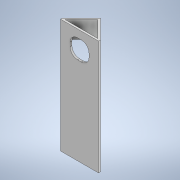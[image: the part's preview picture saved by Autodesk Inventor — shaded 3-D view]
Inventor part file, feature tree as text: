
AUTODESK INVENTOR PART (.ipt)
format: ipt  version: 2020 (Build 240168000, 168)  size: 140,288 bytes
history: native  units: mm
features: extrude x3, sketch x3
ambient origin geometry x8: Origin, YZ Plane, XZ Plane, XY Plane, X Axis, Y Axis, Z Axis, Center Point
bodies: Solid1 (feature_tree)
feature tree (6):
  extrude  "Extrusion1"  Depth=300.0mm
  extrude  "Extrusion2"  TaperAngle=45.0deg  [1 undecoded]
  extrude  "Extrusion6"  Depth=5.0mm
  sketch  "Sketch1"  dims[d0=100.0mm d1=300.0mm]
  sketch  "Sketch2"  dims[d2=5.0mm d3=0.0mm d4=45.0deg]
  sketch  "Sketch6"  dims[d5=5.0mm d6=5.0mm d7=45.0mm d8=0.0mm d21=50.0mm d22=50.0mm d23=20.0mm d24=5.0mm d25=0.0mm]
note: 1 required parameter value undecoded (feature->parameter linkage not recoverable at this tier; creation-order binding heuristic only, values carry confidence <= 0.55)
